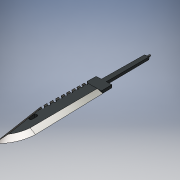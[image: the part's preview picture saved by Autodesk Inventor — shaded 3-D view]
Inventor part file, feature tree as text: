
AUTODESK INVENTOR PART (.ipt)
format: ipt  version: 2018 (Build 220112000, 112)  size: 358,912 bytes
history: native  units: mm
features: chamfer x11, other x7, extrude x3, sketch x3
ambient origin geometry x8: Origin, YZ Plane, XZ Plane, XY Plane, X Axis, Y Axis, Z Axis, Center Point
bodies: Body1 (feature_tree), Body2 (feature_tree)
feature tree (24):
  other  "Těleso1"
  other  "Pracovní rovina3"
  extrude  "Knife"  Depth=11.0mm TaperAngle=45.0deg
  other  "Pracovní rovina4"
  other  "Rozdělit1"
  chamfer  "Zkosení103"  Distance=11.0mm Angle=45.0deg
  chamfer  "Zkosení104"  Distance=11.0mm Angle=45.0deg
  chamfer  "Zkosení105"  Distance=11.0mm Angle=45.0deg
  chamfer  "Zkosení106"  Distance=5.0mm Angle=45.0deg
  chamfer  "Zkosení107"  Distance=2.0mm Angle=45.0deg
  chamfer  "Zkosení108"  Distance=5.0mm Angle=45.0deg
  chamfer  "Zkosení109"  Distance=2.0mm Angle=45.0deg
  chamfer  "Zkosení110"  Distance=2.0mm Angle=45.0deg
  chamfer  "Zkosení111"  Distance=2.0mm Angle=45.0deg
  chamfer  "Zkosení112"  Distance=6.0mm
  extrude  "Teeth"  Depth=10.0mm TaperAngle=45.0deg
  extrude  "Thread"  Depth=10.0mm TaperAngle=0.0deg
  chamfer  "Zkosení113"  [1 undecoded]
  other  "Závit3"
  sketch  "sketch_Knife"  dims[d377=6.0mm d378=0.0mm d379=11.0mm d380=3.0mm d381=45.0deg d382=11.0mm d383=3.0mm d384=45.0deg d385=11.0mm d386=3.0mm d387=45.0deg d388=11.0mm d389=3.0mm d390=45.0deg d391=5.0mm d392=3.0mm d393=45.0deg d394=7.0mm d395=2.0mm d396=45.0deg d397=5.0mm d398=3.0mm d399=45.0deg d400=7.0mm d401=2.0mm d402=45.0deg d405=2.0mm d406=1.0mm d407=45.0deg d408=2.0mm d409=1.0mm d410=45.0deg]
  sketch  "sketch_Teeth"  dims[d469=90.0mm d471=10.0mm d472=10.0mm d474=10.0mm d476=6.0mm d477=0.0mm]
  sketch  "sketch_Thread"  dims[d480=10.0mm d481=0.0mm d484=0.5mm d485=1.0mm d486=45.0deg d488=10.0mm d489=0.0mm]
  other  "Těleso2"
  other  "Těleso3"
note: 1 required parameter value undecoded (feature->parameter linkage not recoverable at this tier; creation-order binding heuristic only, values carry confidence <= 0.55)
